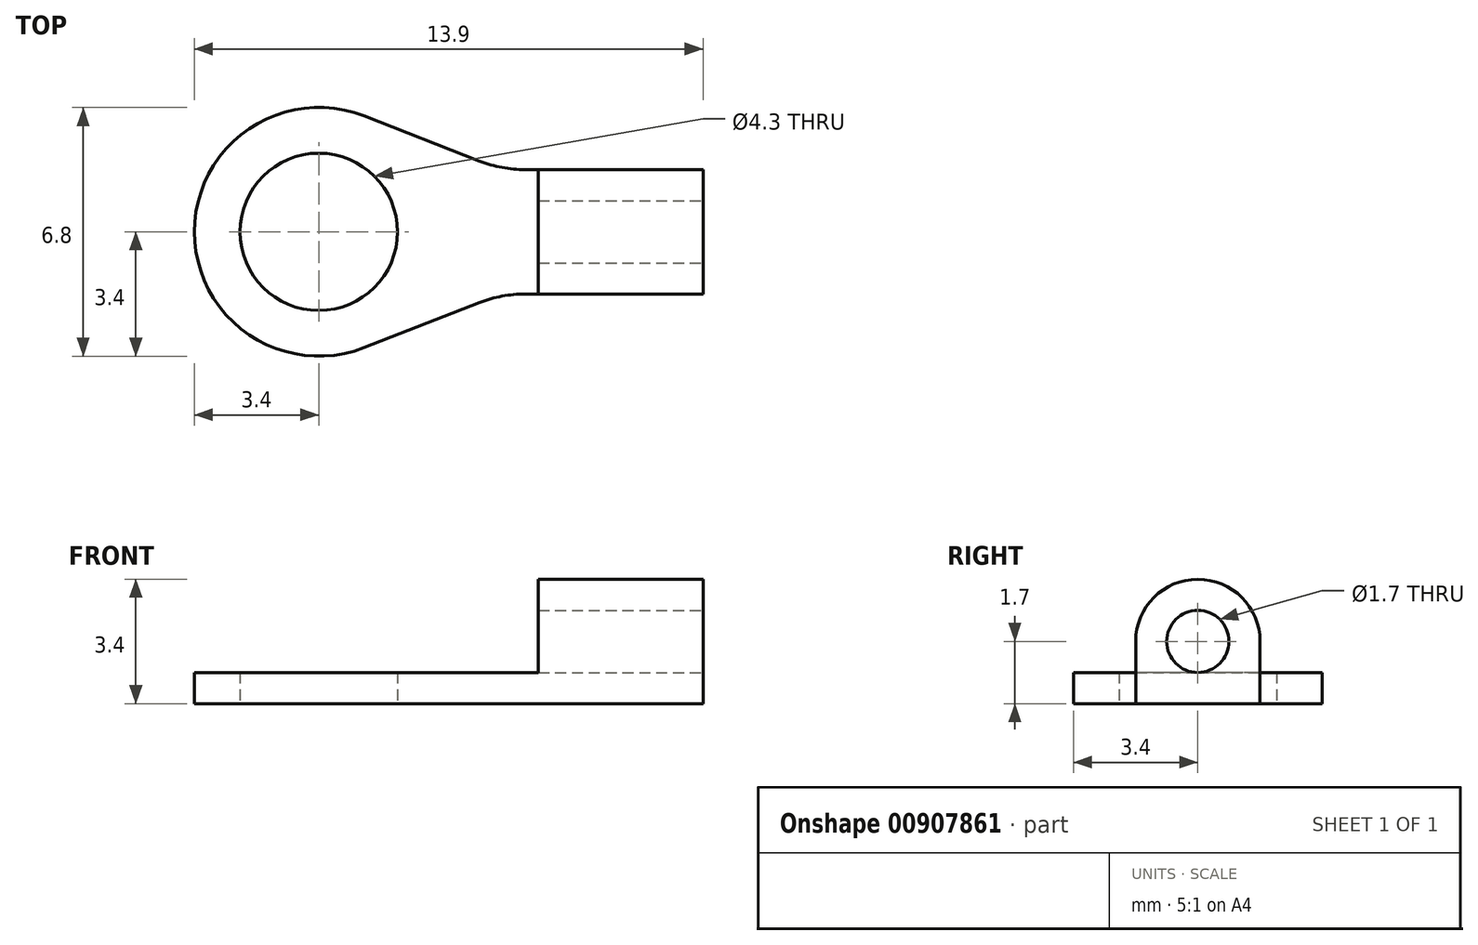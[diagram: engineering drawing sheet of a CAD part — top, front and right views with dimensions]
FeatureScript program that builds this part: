
annotation { "Feature Type Name" : "Feature", "Feature Type Description" : "" }
export const myFeature = defineFeature(function(context is Context, id is Id, definition is map)
    precondition{}
    {
        {
            var Q0;
            Q0=qCreatedBy(makeId("Top.planeOp"),FACE);
            var sketch = newSketch(context, id + "F0", { "sketchPlane" : qUnion([Q0])});
            skLineSegment(sketch, "E0.left", {"start": v(0, 3.4) * mm, "end": v(0, 3.4) * mm});
            skLineSegment(sketch, "E0.right", {"start": v(13.9, 1.7) * mm, "end": v(13.9, 5.1) * mm});
            skPoint(sketch, "E1.visualSharp", {"position": v(0, 6.8) * mm});
            skArc(sketch, "E1.filletArc", {"start": v(3.4, 6.8) * mm, "mid": v(1, 5.8) * mm, "end": v(0, 3.4) * mm});
            skPoint(sketch, "E2.visualSharp", {"position": v(0, 0) * mm});
            skArc(sketch, "E2.filletArc", {"start": v(0, 3.4) * mm, "mid": v(1, 1) * mm, "end": v(3.4, 0) * mm});
            skLineSegment(sketch, "E3.bottom", {"start": v(13.9, 1.7) * mm, "end": v(9.04, 1.7) * mm});
            skLineSegment(sketch, "E3.top", {"start": v(13.9, 5.1) * mm, "end": v(9.04, 5.1) * mm});
            skPoint(sketch, "E3.middle", {"position": v(13.9, 3.4) * mm});
            skArc(sketch, "E4", {"start": v(4.63, 6.57) * mm, "mid": v(0, 3.4) * mm, "end": v(4.63, 0.23) * mm});
            skCircle(sketch, "E5", {"center": v(3.4, 3.4) * mm, "radius": 2.15 * mm});
            skLineSegment(sketch, "E6", {"start": v(7.8, 5.33) * mm, "end": v(4.63, 6.57) * mm});
            skLineSegment(sketch, "E7", {"start": v(7.8, 1.47) * mm, "end": v(4.63, 0.23) * mm});
            skPoint(sketch, "E8.orphan", {"position": v(18.4, 5.1) * mm});
            skPoint(sketch, "E9.orphan", {"position": v(18.4, 1.7) * mm});
            skPoint(sketch, "E0.top.end.orphan", {"position": v(13.9, 6.8) * mm});
            skPoint(sketch, "E0.bottom.end.orphan", {"position": v(13.9, 0) * mm});
            skPoint(sketch, "E3.right.end.orphan", {"position": v(9.4, 5.1) * mm});
            skPoint(sketch, "E3.right.start.orphan", {"position": v(9.4, 1.7) * mm});
            skPoint(sketch, "E10.visualSharp", {"position": v(8.4, 5.1) * mm});
            skArc(sketch, "E10.filletArc", {"start": v(7.8, 5.33) * mm, "mid": v(8.41, 5.16) * mm, "end": v(9.04, 5.1) * mm});
            skPoint(sketch, "E11.visualSharp", {"position": v(8.4, 1.7) * mm});
            skArc(sketch, "E11.filletArc", {"start": v(9.04, 1.7) * mm, "mid": v(8.41, 1.64) * mm, "end": v(7.8, 1.47) * mm});
            skSolve(sketch);
        }
        {
            var Q0;
            Q0=makeQuery(id+"F0.imprint","IMPRINT",FACE,{"disambiguationData":[TD([[makeQuery(id+"F0.imprint","IMPRINT",EDGE,{"derivedFrom":sQuery(id+"F0.wireOp",EDGE,"E0.right")}),1.0]])]});
            extrude(context, id + "F1", {"entities" : qUnion([Q0]), "depth" : 0.85 * mm, "offsetDistance" : 25 * mm});
        }
        {
            var Q0;
            Q0=makeQuery(id+"F1.opExtrude","CAP_FACE",FACE,{"disambiguationData":[OSD([sQuery(id+"F0.wireOp",EDGE,"E0.right"),sQuery(id+"F0.wireOp",EDGE,"E3.bottom"),sQuery(id+"F0.wireOp",EDGE,"E3.top"),sQuery(id+"F0.wireOp",EDGE,"E4"),sQuery(id+"F0.wireOp",EDGE,"E5"),sQuery(id+"F0.wireOp",EDGE,"E6"),sQuery(id+"F0.wireOp",EDGE,"E7"),sQuery(id+"F0.wireOp",EDGE,"E10.filletArc"),sQuery(id+"F0.wireOp",EDGE,"E11.filletArc")])],"isStart":false});
            var sketch = newSketch(context, id + "F2", { "sketchPlane" : qUnion([Q0])});
            skLineSegment(sketch, "E12.bottom", {"start": v(13.9, 5.1) * mm, "end": v(9.4, 5.1) * mm});
            skLineSegment(sketch, "E12.top", {"start": v(13.9, 1.7) * mm, "end": v(9.4, 1.7) * mm});
            skLineSegment(sketch, "E12.left", {"start": v(13.9, 5.1) * mm, "end": v(13.9, 1.7) * mm});
            skLineSegment(sketch, "E12.right", {"start": v(9.4, 5.1) * mm, "end": v(9.4, 1.7) * mm});
            skSolve(sketch);
        }
        {
            var Q0;
            Q0=makeQuery(id+"F2.imprint","IMPRINT",FACE,{"disambiguationData":[TD([[makeQuery(id+"F2.imprint","IMPRINT",EDGE,{"derivedFrom":sQuery(id+"F2.wireOp",EDGE,"E12.bottom")}),1.0]])]});
            extrude(context, id + "F3", {"entities" : qUnion([Q0]), "operationType" : NewBodyOperationType.ADD, "depth" : 2.55 * mm, "offsetDistance" : 25 * mm});
        }
        {
            var Q0;
            Q0=makeQuery(id+"F3.opExtrude","CAP_EDGE",EDGE,{"disambiguationData":[OSD([sQuery(id+"F2.wireOp",EDGE,"E12.bottom")])],"isStart":false});
            var Q1;
            Q1=makeQuery(id+"F3.opExtrude","CAP_EDGE",EDGE,{"disambiguationData":[OSD([sQuery(id+"F2.wireOp",EDGE,"E12.top")])],"isStart":false});
            fillet(context, id + "F4", {"entities" : qUnion([Q0, Q1]), "radius" : 1.7 * mm, "tangentPropagation" : true, "allowEdgeOverflow" : false});
        }
        {
            var Q0;
            Q0=makeQuery(id+"F3.boolean.opBoolean","MERGE",FACE,{"derivedFrom":[makeQuery(id+"F1.opExtrude","SWEPT_FACE",FACE,{"disambiguationData":[OSD([sQuery(id+"F0.wireOp",EDGE,"E0.right")])]}),makeQuery(id+"F3.opExtrude","SWEPT_FACE",FACE,{"disambiguationData":[OSD([sQuery(id+"F2.wireOp",EDGE,"E12.left")])]})]});
            var sketch = newSketch(context, id + "F5", { "sketchPlane" : qUnion([Q0])});
            skCircle(sketch, "E13", {"center": v(3.4, 1.7) * mm, "radius": 0.85 * mm});
            skSolve(sketch);
        }
        {
            var Q0;
            Q0=makeQuery(id+"F5.imprint","IMPRINT",FACE,{"disambiguationData":[TD([[makeQuery(id+"F5.imprint","IMPRINT",EDGE,{"derivedFrom":sQuery(id+"F5.wireOp",EDGE,"E13")}),1.0]])]});
            extrude(context, id + "F6", {"entities" : qUnion([Q0]), "operationType" : NewBodyOperationType.REMOVE, "oppositeDirection" : true, "depth" : 25 * mm, "offsetDistance" : 25 * mm});
        }
    });
